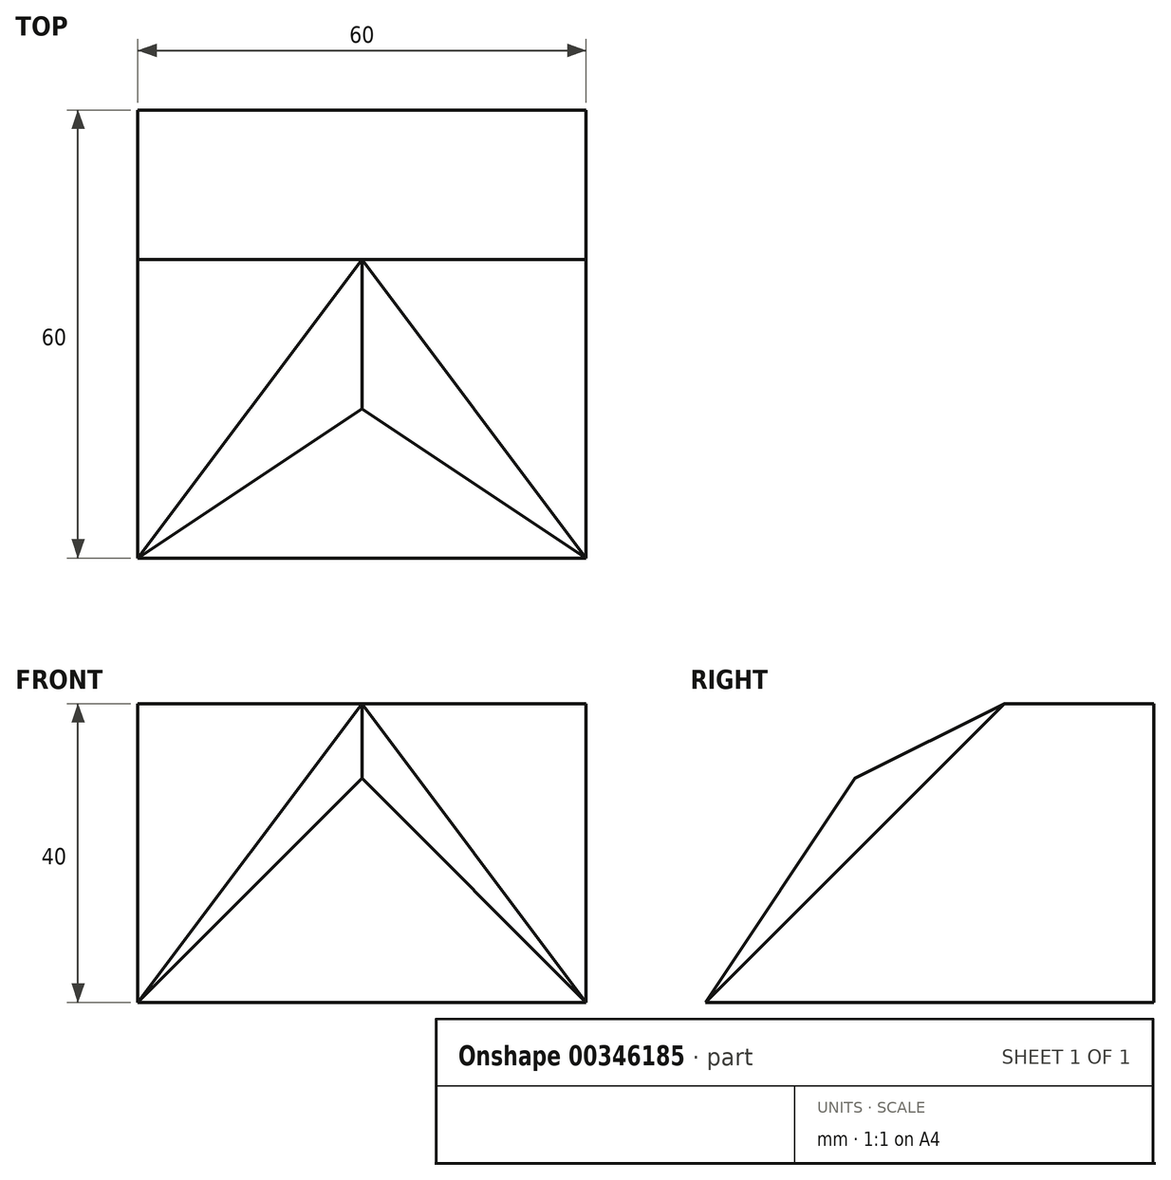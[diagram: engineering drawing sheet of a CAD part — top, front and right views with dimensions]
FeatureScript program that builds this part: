
annotation { "Feature Type Name" : "Feature", "Feature Type Description" : "" }
export const myFeature = defineFeature(function(context is Context, id is Id, definition is map)
    precondition{}
    {
        {
            var Q0;
            Q0=qCreatedBy(makeId("Top.planeOp"),FACE);
            var sketch = newSketch(context, id + "F0", { "sketchPlane" : qUnion([Q0])});
            skLineSegment(sketch, "E0.bottom", {"start": v(30, -30) * mm, "end": v(-30, -30) * mm});
            skLineSegment(sketch, "E0.top", {"start": v(30, 30) * mm, "end": v(-30, 30) * mm});
            skLineSegment(sketch, "E0.left", {"start": v(30, -30) * mm, "end": v(30, 30) * mm});
            skLineSegment(sketch, "E0.right", {"start": v(-30, -30) * mm, "end": v(-30, 30) * mm});
            skPoint(sketch, "E0.middle", {"position": v(0, 0) * mm});
            skSolve(sketch);
        }
        {
            var Q0;
            Q0=qCreatedBy(makeId("Top.planeOp"),FACE);
            cPlane(context, id + "F1", {"entities" : qUnion([Q0]), "cplaneType" : CPlaneType.OFFSET, "offset" : 40 * mm, "width" : 150 * mm, "height" : 150 * mm});
        }
        {
            var Q0;
            Q0=qCreatedBy(id+"F1.planeOp",FACE);
            var sketch = newSketch(context, id + "F2", { "sketchPlane" : qUnion([Q0])});
            skLineSegment(sketch, "E1.bottom", {"start": v(-30, 30) * mm, "end": v(30, 30) * mm});
            skLineSegment(sketch, "E1.top", {"start": v(-30, 10) * mm, "end": v(30, 10) * mm});
            skLineSegment(sketch, "E1.left", {"start": v(-30, 30) * mm, "end": v(-30, 10) * mm});
            skLineSegment(sketch, "E1.right", {"start": v(30, 30) * mm, "end": v(30, 10) * mm});
            skSolve(sketch);
        }
        {
            var Q0;
            Q0=makeQuery(id+"F0.imprint","IMPRINT",FACE,{"disambiguationData":[TD([[makeQuery(id+"F0.imprint","IMPRINT",EDGE,{"derivedFrom":sQuery(id+"F0.wireOp",EDGE,"E0.bottom")}),-1.0]])]});
            var Q1;
            Q1=makeQuery(id+"F2.imprint","IMPRINT",FACE,{"disambiguationData":[TD([[makeQuery(id+"F2.imprint","IMPRINT",EDGE,{"derivedFrom":sQuery(id+"F2.wireOp",EDGE,"E1.bottom")}),-1.0]])]});
            loft(context, id + "F3", {"sheetProfilesArray" : [{ "sheetProfileEntities" : qUnion([Q0]) }, { "sheetProfileEntities" : qUnion([Q1]) }]});
        }
        {
            var Q0;
            Q0=makeQuery(id+"F3.opLoft","SWEPT_FACE",FACE,{"disambiguationData":[OSD([sQuery(id+"F0.wireOp",EDGE,"E0.bottom"),sQuery(id+"F0.wireOp",EDGE,"E0.left"),sQuery(id+"F0.wireOp",EDGE,"E0.right"),sQuery(id+"F2.wireOp",EDGE,"E1.top"),sQuery(id+"F2.wireOp",EDGE,"E1.left"),sQuery(id+"F2.wireOp",EDGE,"E1.right")])]});
            var sketch = newSketch(context, id + "F4", { "sketchPlane" : qUnion([Q0])});
            skLineSegment(sketch, "E2", {"start": v(-30, -21.21) * mm, "end": v(0, 35.36) * mm});
            skLineSegment(sketch, "E3", {"start": v(0, 35.36) * mm, "end": v(30, -21.21) * mm});
            skSolve(sketch);
        }
        {
            var Q0;
            Q0=qCreatedBy(makeId("Right.planeOp"),FACE);
            var sketch = newSketch(context, id + "F5", { "sketchPlane" : qUnion([Q0])});
            skPoint(sketch, "E4", {"position": v(-10, 30) * mm});
            skSolve(sketch);
        }
        {
            var Q1;
            Q1=makeQuery(id+"F4.imprint","IMPRINT",FACE,{"disambiguationData":[TD([[makeQuery(id+"F4.imprint","IMPRINT",EDGE,{"derivedFrom":sQuery(id+"F4.wireOp",EDGE,"E2")}),-1.0]])]});
            var Q2;
            Q2=sQuery(id+"F5.wireOp",VERTEX,"E4");
            loft(context, id + "F6", {"operationType" : NewBodyOperationType.ADD, "sheetProfilesArray" : [{ "sheetProfileEntities" : qUnion([Q1]) }, { "sheetProfileEntities" : qUnion([Q2]) }]});
        }
    });
